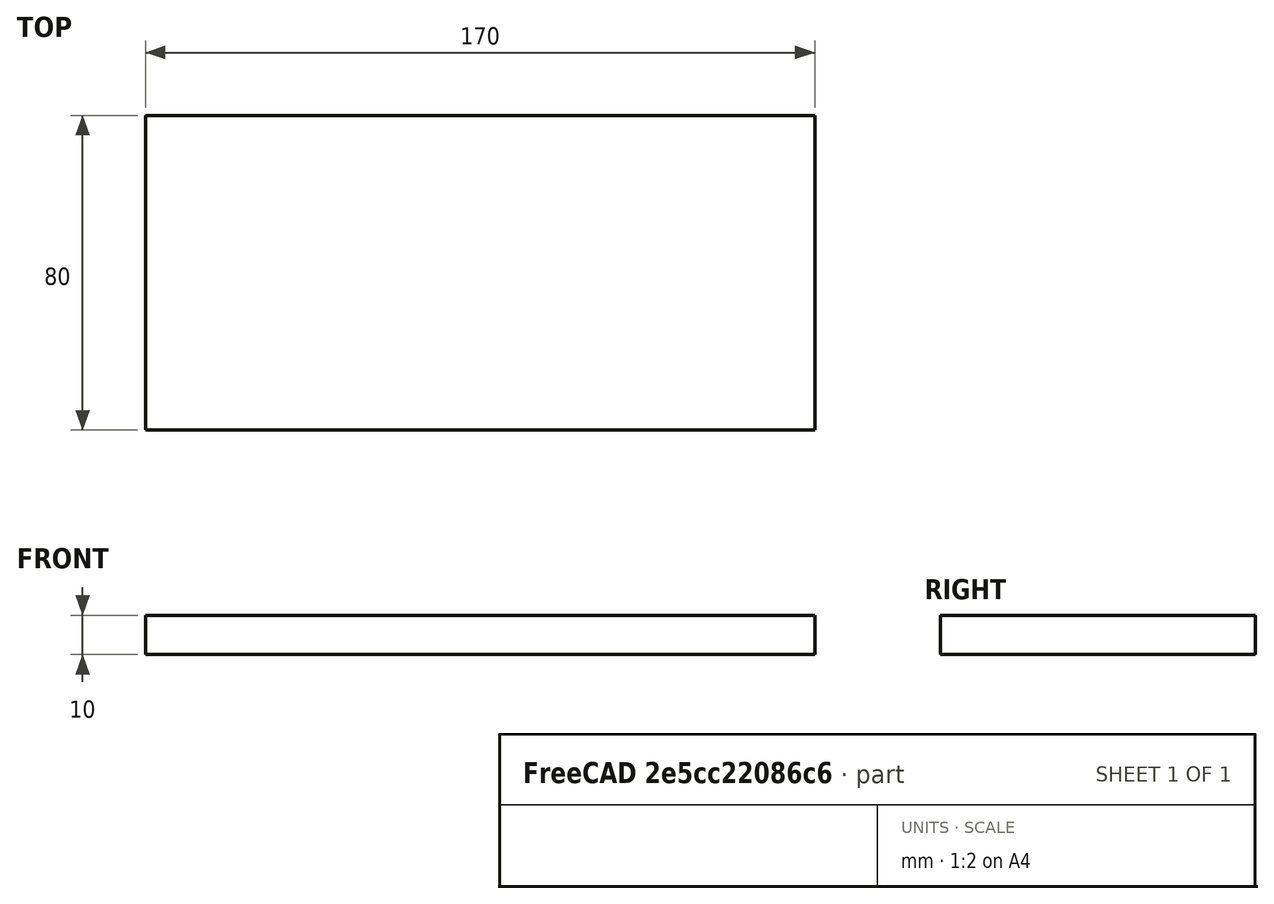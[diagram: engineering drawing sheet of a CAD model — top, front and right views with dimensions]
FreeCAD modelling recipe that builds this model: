
FCSTD DOCUMENT  (FreeCAD 0.18R4 (GitTag))
Label: Divider-B
License: All rights reserved
LicenseURL: http://en.wikipedia.org/wiki/All_rights_reserved
objects: Sketcher::SketchObject×1, PartDesign::Pad×1, PartDesign::Body×1
note: 4 computed .brp shape members not serialized (recipe doc carries the construction recipe); baked Part::Feature solids carry a one-line shape summary decoded from their .brp

FEATURE [Sketcher::SketchObject] Sketch
  MapMode = 5
  Support = -> [XY_Plane]
  sketch-geometry (4):
    g0: LineSegment StartX=0 StartY=0 StartZ=0 EndX=-170 EndY=0 EndZ=0
    g1: LineSegment StartX=-170 StartY=0 StartZ=0 EndX=-170 EndY=80 EndZ=0
    g2: LineSegment StartX=-170 StartY=80 StartZ=0 EndX=0 EndY=80 EndZ=0
    g3: LineSegment StartX=0 StartY=80 StartZ=0 EndX=0 EndY=0 EndZ=0
  constraints (11):
    c: Coincident(g0,g1)
    c: Coincident(g1,g2)
    c: Coincident(g2,g3)
    c: Coincident(g3,g0)
    c: Horizontal(g0)
    c: Horizontal(g2)
    c: Vertical(g1)
    c: Vertical(g3)
    c: Distance(g2) = 170
    c: Distance(g3) = 80
    c: Coincident(g0,g-1)
FEATURE [PartDesign::Pad] Pad
  Length = 10
  Length2 = 100
  Profile = -> Sketch
  Type = 0
FEATURE [PartDesign::Body] Body
  Group = -> [Sketch,Pad]
  Origin = -> Origin
  Tip = -> Pad
